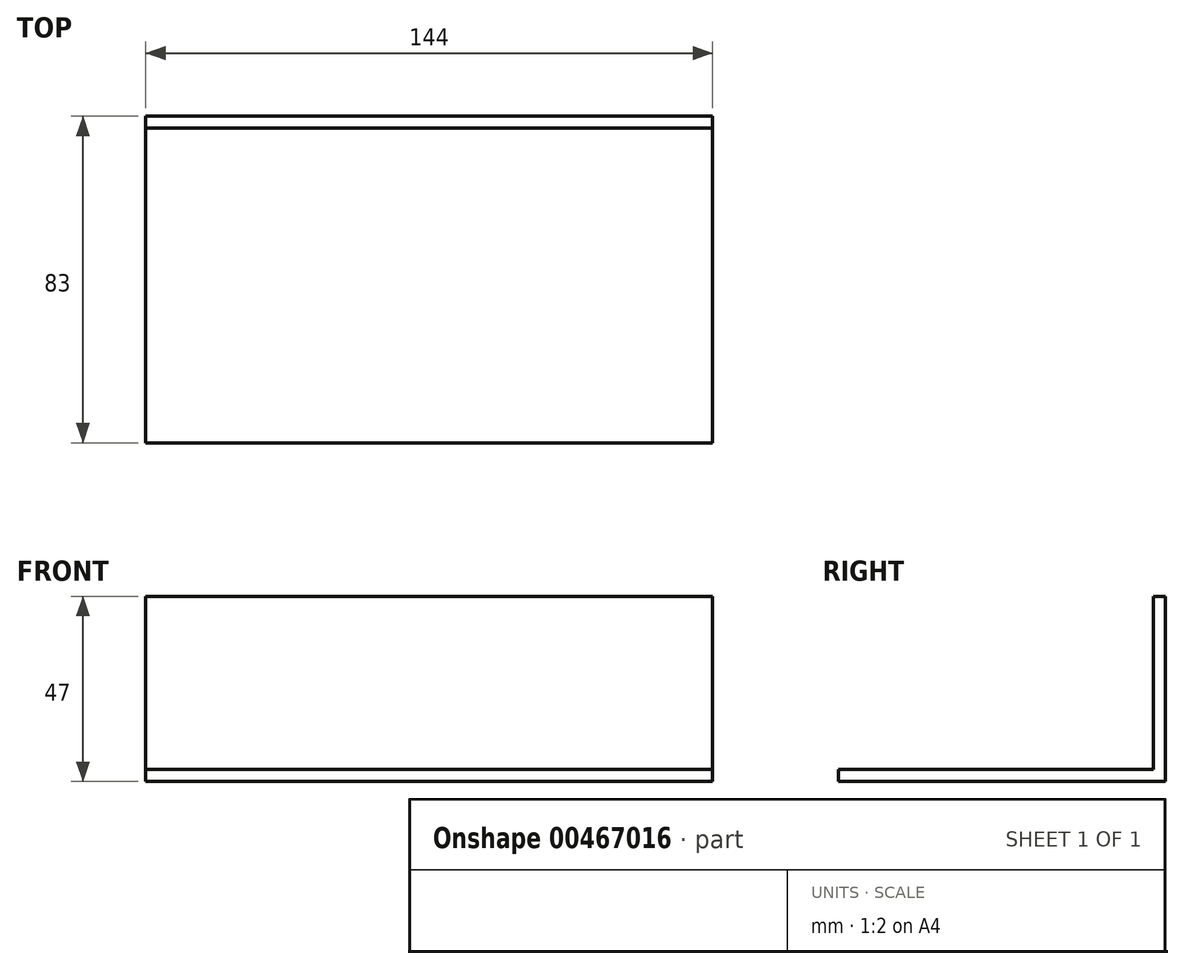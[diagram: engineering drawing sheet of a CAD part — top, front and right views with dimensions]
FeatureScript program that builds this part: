
annotation { "Feature Type Name" : "Feature", "Feature Type Description" : "" }
export const myFeature = defineFeature(function(context is Context, id is Id, definition is map)
    precondition{}
    {
        {
            assignVariable(context, id + "F0", {"name" : "szer", "anyValue" : 3});
        }
        {
            var Q0;
            Q0=qCreatedBy(makeId("Top.planeOp"),FACE);
            var sketch = newSketch(context, id + "F1", { "sketchPlane" : qUnion([Q0])});
            skLineSegment(sketch, "E0", {"start": v(0, 0) * mm, "end": v(144, 0) * mm});
            skLineSegment(sketch, "E1", {"start": v(144, 0) * mm, "end": v(144, 80) * mm});
            skLineSegment(sketch, "E2", {"start": v(144, 80) * mm, "end": v(123.38, 80) * mm});
            skLineSegment(sketch, "E3", {"start": v(123.38, 80) * mm, "end": v(123.38, 83) * mm});
            skLineSegment(sketch, "E4", {"start": v(123.38, 83) * mm, "end": v(84.27, 83) * mm});
            skLineSegment(sketch, "E5", {"start": v(84.27, 83) * mm, "end": v(84.27, 80) * mm});
            skLineSegment(sketch, "E6", {"start": v(84.27, 80) * mm, "end": v(50.13, 80) * mm});
            skLineSegment(sketch, "E7", {"start": v(50.13, 80) * mm, "end": v(50.13, 83) * mm});
            skLineSegment(sketch, "E8", {"start": v(50.13, 83) * mm, "end": v(11.02, 83) * mm});
            skLineSegment(sketch, "E9", {"start": v(11.02, 83) * mm, "end": v(11.02, 80) * mm});
            skLineSegment(sketch, "E10", {"start": v(11.02, 80) * mm, "end": v(0, 80) * mm});
            skLineSegment(sketch, "E11", {"start": v(0, 80) * mm, "end": v(0, 0) * mm});
            skSolve(sketch);
        }
        {
            var Q0;
            Q0=makeQuery(id+"F1.imprint","IMPRINT",FACE,{"disambiguationData":[TD([[makeQuery(id+"F1.imprint","IMPRINT",EDGE,{"derivedFrom":sQuery(id+"F1.wireOp",EDGE,"E0")}),1.0]])]});
            extrude(context, id + "F2", {"entities" : qUnion([Q0]), "depth" : (getVariable(context, 'szer')) * mm});
        }
        {
            var Q0;
            Q0=makeQuery(id+"F2.opExtrude","CAP_FACE",FACE,{"disambiguationData":[OSD([sQuery(id+"F1.wireOp",EDGE,"E0"),sQuery(id+"F1.wireOp",EDGE,"E1"),sQuery(id+"F1.wireOp",EDGE,"E2"),sQuery(id+"F1.wireOp",EDGE,"E3"),sQuery(id+"F1.wireOp",EDGE,"E4"),sQuery(id+"F1.wireOp",EDGE,"E5"),sQuery(id+"F1.wireOp",EDGE,"E6"),sQuery(id+"F1.wireOp",EDGE,"E7"),sQuery(id+"F1.wireOp",EDGE,"E8"),sQuery(id+"F1.wireOp",EDGE,"E9"),sQuery(id+"F1.wireOp",EDGE,"E10"),sQuery(id+"F1.wireOp",EDGE,"E11")])],"isStart":false});
            var sketch = newSketch(context, id + "F3", { "sketchPlane" : qUnion([Q0])});
            skLineSegment(sketch, "E12", {"start": v(0, 80) * mm, "end": v(144, 80) * mm});
            skLineSegment(sketch, "E13", {"start": v(144, 80) * mm, "end": v(144, 83) * mm});
            skLineSegment(sketch, "E14", {"start": v(144, 83) * mm, "end": v(0, 83) * mm});
            skLineSegment(sketch, "E15", {"start": v(0, 83) * mm, "end": v(0, 80) * mm});
            skSolve(sketch);
        }
        {
            var Q0;
            {var subQ0=sQuery(id+"F3.wireOp",EDGE,"E13");Q0=makeQuery(id+"F3.imprint","IMPRINT",FACE,{"disambiguationData":[TD([[makeQuery(id+"F3.imprint","IMPRINT",EDGE,{"derivedFrom":subQ0}),1.0]])]});}
            var Q1;
            {var subQ1=makeQuery(id+"F2.opExtrude","CAP_EDGE",EDGE,{"disambiguationData":[OSD([sQuery(id+"F1.wireOp",EDGE,"E3")])],"isStart":false});Q1=makeQuery(id+"F3.imprint","IMPRINT",FACE,{"disambiguationData":[TD([[makeQuery(id+"F3.imprint","IMPRINT",EDGE,{"derivedFrom":subQ1}),1.0]])]});}
            var Q2;
            {var subQ1=makeQuery(id+"F2.opExtrude","CAP_EDGE",EDGE,{"disambiguationData":[OSD([sQuery(id+"F1.wireOp",EDGE,"E7")])],"isStart":false});Q2=makeQuery(id+"F3.imprint","IMPRINT",FACE,{"disambiguationData":[TD([[makeQuery(id+"F3.imprint","IMPRINT",EDGE,{"derivedFrom":subQ1}),1.0]])]});}
            var Q3;
            {var subQ2=sQuery(id+"F3.wireOp",EDGE,"E15");Q3=makeQuery(id+"F3.imprint","IMPRINT",FACE,{"disambiguationData":[TD([[makeQuery(id+"F3.imprint","IMPRINT",EDGE,{"derivedFrom":subQ2}),1.0]])]});}
            var Q4;
            {var subQ1=makeQuery(id+"F2.opExtrude","CAP_EDGE",EDGE,{"disambiguationData":[OSD([sQuery(id+"F1.wireOp",EDGE,"E5")])],"isStart":false});Q4=makeQuery(id+"F3.imprint","IMPRINT",FACE,{"disambiguationData":[TD([[makeQuery(id+"F3.imprint","IMPRINT",EDGE,{"derivedFrom":subQ1}),-1.0]])]});}
            extrude(context, id + "F4", {"entities" : qUnion([Q0, Q1, Q2, Q3, Q4]), "depth" : 44 * mm});
        }
        {
            var Q0;
            {var subQ2=sQuery(id+"F3.wireOp",EDGE,"E15");Q0=makeQuery(id+"F3.imprint","IMPRINT",FACE,{"disambiguationData":[TD([[makeQuery(id+"F3.imprint","IMPRINT",EDGE,{"derivedFrom":subQ2}),1.0]])]});}
            var Q1;
            {var subQ1=makeQuery(id+"F2.opExtrude","CAP_EDGE",EDGE,{"disambiguationData":[OSD([sQuery(id+"F1.wireOp",EDGE,"E5")])],"isStart":false});Q1=makeQuery(id+"F3.imprint","IMPRINT",FACE,{"disambiguationData":[TD([[makeQuery(id+"F3.imprint","IMPRINT",EDGE,{"derivedFrom":subQ1}),-1.0]])]});}
            var Q2;
            {var subQ0=sQuery(id+"F3.wireOp",EDGE,"E13");Q2=makeQuery(id+"F3.imprint","IMPRINT",FACE,{"disambiguationData":[TD([[makeQuery(id+"F3.imprint","IMPRINT",EDGE,{"derivedFrom":subQ0}),1.0]])]});}
            extrude(context, id + "F5", {"entities" : qUnion([Q0, Q1, Q2]), "operationType" : NewBodyOperationType.ADD, "oppositeDirection" : true, "depth" : (getVariable(context, 'szer')) * mm});
        }
    });
